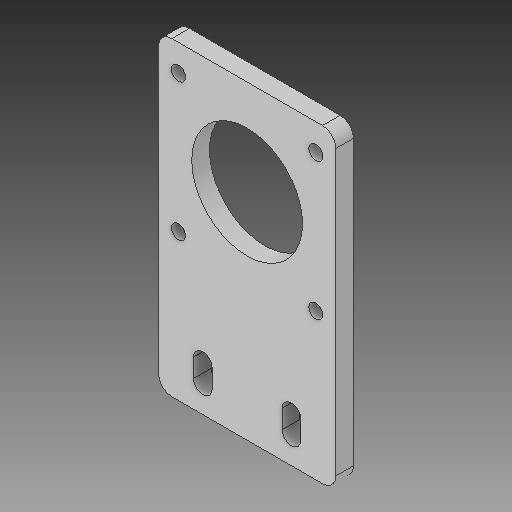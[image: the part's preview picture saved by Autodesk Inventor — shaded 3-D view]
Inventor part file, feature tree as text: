
AUTODESK INVENTOR PART (.ipt)
format: ipt  version: 2018 (Build 220112000, 112)  size: 146,432 bytes
history: native  units: mm
features: extrude x3, sketch x3, fillet x1
ambient origin geometry x8: Origin, YZ Plane, XZ Plane, XY Plane, X Axis, Y Axis, Z Axis, Center Point
bodies: Solid1 (feature_tree)
feature tree (7):
  extrude  "Extrusion1"  Depth=70.0mm
  extrude  "Extrusion2"  Depth=4.0mm
  extrude  "Extrusion3"  Depth=3.0mm
  fillet  "Fillet1"  Radius=21.5mm
  sketch  "Sketch1"  dims[d0=40.0mm d1=70.0mm]
  sketch  "Sketch2"  dims[d2=4.0mm d3=0.0mm d4=3.2mm]
  sketch  "Sketch3"  dims[d5=31.0mm d6=31.0mm d7=21.5mm d8=25.0mm d9=4.0mm d10=0.0mm d11=4.2mm d12=4.2mm d13=20.0mm d14=6.0mm d15=4.0mm d16=0.0mm d17=3.0mm]
